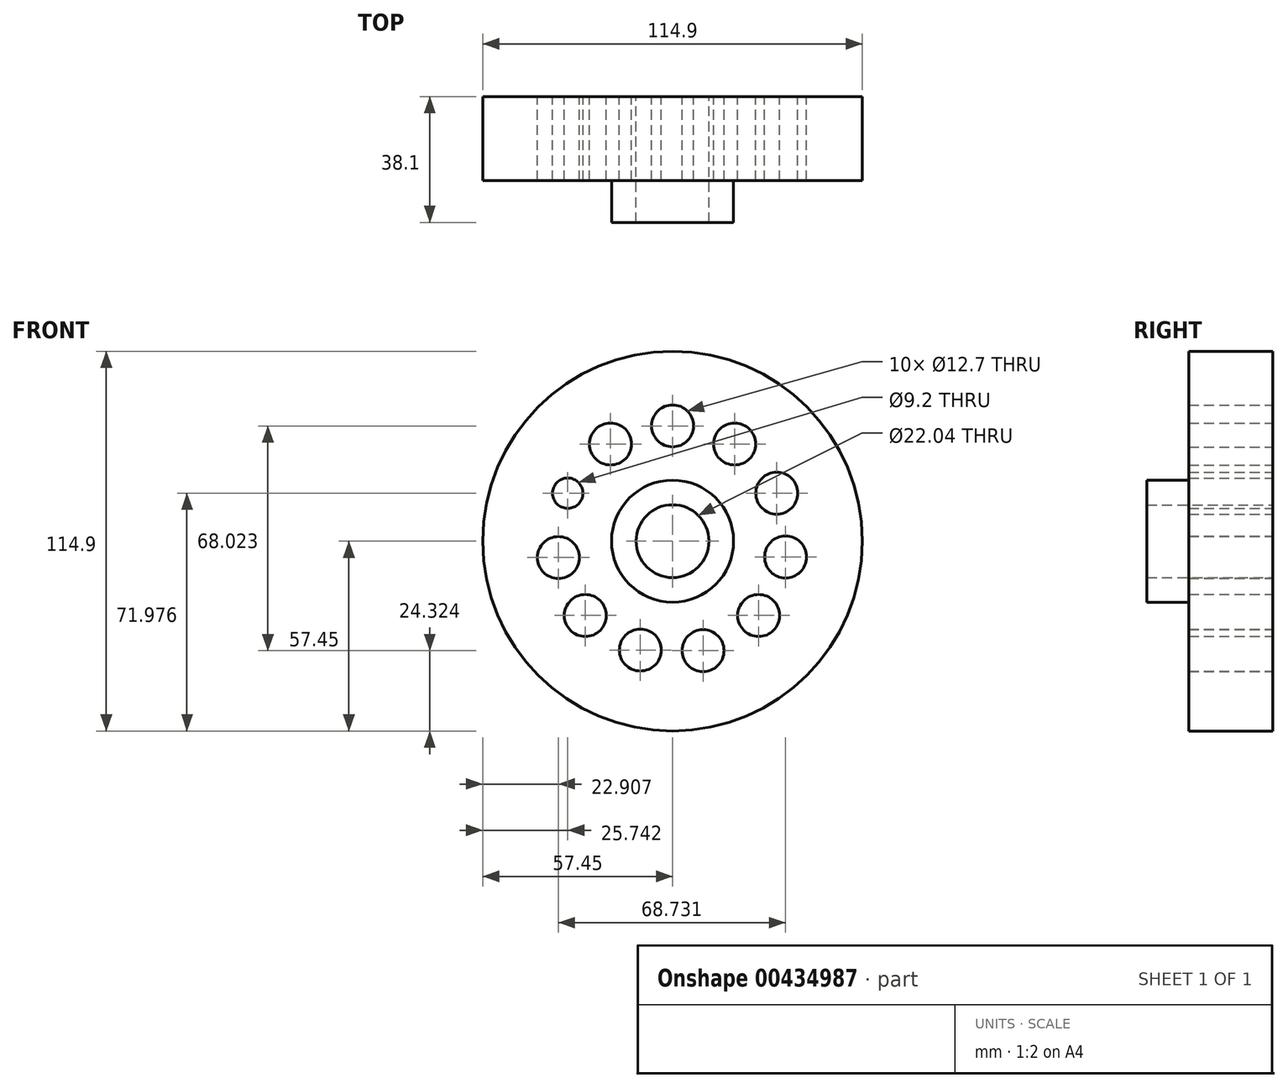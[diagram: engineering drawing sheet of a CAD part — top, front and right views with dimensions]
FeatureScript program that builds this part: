
annotation { "Feature Type Name" : "Feature", "Feature Type Description" : "" }
export const myFeature = defineFeature(function(context is Context, id is Id, definition is map)
    precondition{}
    {
        {
            var Q0;
            Q0=qCreatedBy(makeId("Front.planeOp"),FACE);
            var sketch = newSketch(context, id + "F0", { "sketchPlane" : qUnion([Q0])});
            skCircle(sketch, "E0", {"center": v(0, 0) * mm, "radius": 57.45 * mm});
            skPoint(sketch, "E1", {"position": v(0, 31.74) * mm});
            skPoint(sketch, "E2.1.0", {"position": v(-17.16, 26.7) * mm});
            skPoint(sketch, "E2.2.0", {"position": v(-28.88, 13.19) * mm});
            skPoint(sketch, "E2.3.0", {"position": v(-31.42, -4.52) * mm});
            skPoint(sketch, "E2.4.0", {"position": v(-24, -20.79) * mm});
            skPoint(sketch, "E2.5.0", {"position": v(-8.94, -30.46) * mm});
            skPoint(sketch, "E2.6.0", {"position": v(8.94, -30.46) * mm});
            skPoint(sketch, "E2.7.0", {"position": v(24, -20.79) * mm});
            skPoint(sketch, "E2.8.0", {"position": v(31.42, -4.52) * mm});
            skPoint(sketch, "E2.9.0", {"position": v(28.88, 13.19) * mm});
            skPoint(sketch, "E2.10.0", {"position": v(17.16, 26.7) * mm});
            skSolve(sketch);
        }
        {
            var Q0;
            Q0=makeQuery(id+"F0.imprint","IMPRINT",FACE,{"disambiguationData":[TD([[makeQuery(id+"F0.imprint","IMPRINT",EDGE,{"derivedFrom":sQuery(id+"F0.wireOp",EDGE,"E0")}),1.0]])]});
            var sketch = newSketch(context, id + "F1", { "sketchPlane" : qUnion([Q0])});
            skCircle(sketch, "E3", {"center": v(0, 0) * mm, "radius": 18.39 * mm});
            skCircle(sketch, "E4", {"center": v(0, 0) * mm, "radius": 6.51 * mm});
            skCircle(sketch, "E5", {"center": v(-18.78, 29.4) * mm, "radius": 6.35 * mm});
            skCircle(sketch, "E6", {"center": v(-31.7, 14.53) * mm, "radius": 4.6 * mm});
            skCircle(sketch, "E7", {"center": v(-34.54, -4.96) * mm, "radius": 6.35 * mm});
            skCircle(sketch, "E8", {"center": v(-26.4, -22.5) * mm, "radius": 6.35 * mm});
            skCircle(sketch, "E9", {"center": v(-9.74, -32.95) * mm, "radius": 6.35 * mm});
            skCircle(sketch, "E10", {"center": v(9.21, -33.13) * mm, "radius": 6.35 * mm});
            skCircle(sketch, "E11", {"center": v(26.04, -22.5) * mm, "radius": 6.35 * mm});
            skCircle(sketch, "E12", {"center": v(34.19, -4.78) * mm, "radius": 6.35 * mm});
            skCircle(sketch, "E13", {"center": v(31.53, 14.53) * mm, "radius": 6.35 * mm});
            skCircle(sketch, "E14", {"center": v(18.78, 29.4) * mm, "radius": 6.35 * mm});
            skCircle(sketch, "E15", {"center": v(0, 34.9) * mm, "radius": 6.35 * mm});
            skSolve(sketch);
        }
        {
            var Q0;
            Q0=makeQuery(id+"F1.imprint","IMPRINT",FACE,{"disambiguationData":[TD([[makeQuery(id+"F1.imprint","IMPRINT",EDGE,{"derivedFrom":sQuery(id+"F1.wireOp",EDGE,"E3")}),-1.0]])]});
            extrude(context, id + "F2", {"entities" : qUnion([Q0]), "depth" : 25.4 * mm});
        }
        {
            var Q0;
            Q0=qCreatedBy(makeId("Front.planeOp"),FACE);
            var sketch = newSketch(context, id + "F3", { "sketchPlane" : qUnion([Q0])});
            skCircle(sketch, "E16", {"center": v(0, 0) * mm, "radius": 18.46 * mm});
            skCircle(sketch, "E17", {"center": v(0, 0) * mm, "radius": 11.02 * mm});
            skSolve(sketch);
        }
        {
            var Q0;
            Q0 = qSketchRegion(id + "F3", true);
            extrude(context, id + "F4", {"entities" : qUnion([Q0]), "operationType" : NewBodyOperationType.ADD, "depth" : 38.1 * mm});
        }
    });
